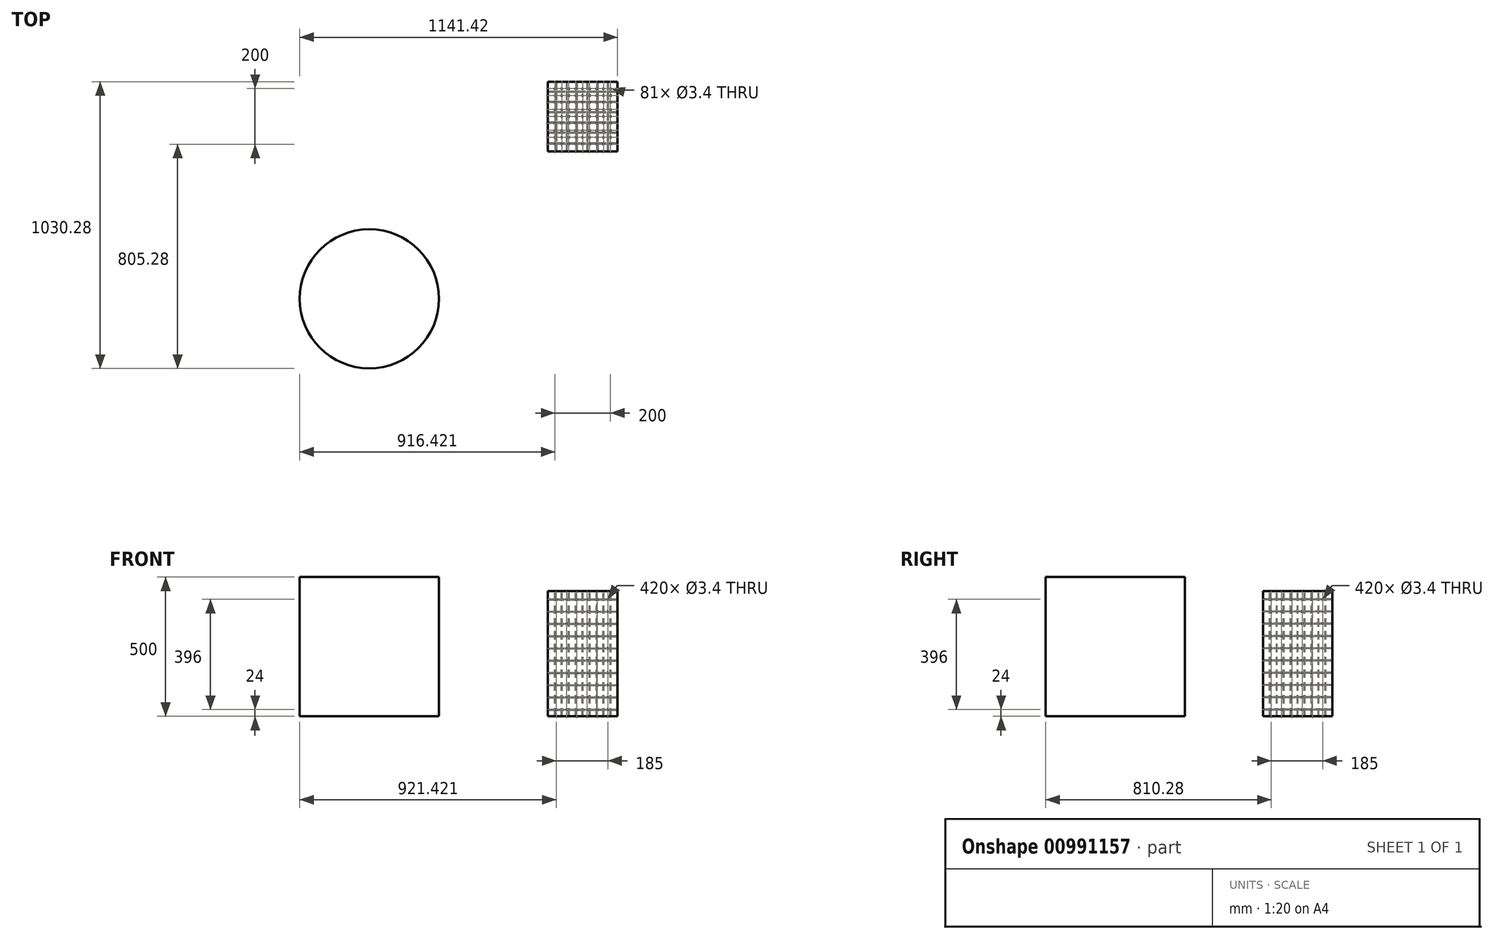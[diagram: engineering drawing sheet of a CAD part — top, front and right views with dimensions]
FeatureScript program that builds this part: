
annotation { "Feature Type Name" : "Feature", "Feature Type Description" : "" }
export const myFeature = defineFeature(function(context is Context, id is Id, definition is map)
    precondition{}
    {
        {
            var Q0;
            Q0=qCreatedBy(makeId("Top.planeOp"),FACE);
            var sketch = newSketch(context, id + "F0", { "sketchPlane" : qUnion([Q0])});
            skLineSegment(sketch, "E0.bottom", {"start": v(256.48, 280.26) * mm, "end": v(6.48, 280.26) * mm});
            skLineSegment(sketch, "E0.top", {"start": v(256.48, 30.26) * mm, "end": v(6.48, 30.26) * mm});
            skLineSegment(sketch, "E0.left", {"start": v(256.48, 280.26) * mm, "end": v(256.48, 30.26) * mm});
            skLineSegment(sketch, "E0.right", {"start": v(6.48, 280.26) * mm, "end": v(6.48, 30.26) * mm});
            skPoint(sketch, "E0.middle", {"position": v(131.48, 155.26) * mm});
            skSolve(sketch);
        }
        {
            var Q0;
            Q0 = qSketchRegion(id + "F0", true);
            extrude(context, id + "F1", {"entities" : qUnion([Q0]), "depth" : 450 * mm, "offsetDistance" : 25 * mm});
        }
        {
            var Q0;
            Q0=makeQuery(id+"F1.opExtrude","SWEPT_FACE",FACE,{"disambiguationData":[OSD([sQuery(id+"F0.wireOp",EDGE,"E0.top")])]});
            var sketch = newSketch(context, id + "F2", { "sketchPlane" : qUnion([Q0])});
            skPoint(sketch, "E1", {"position": v(36.48, 420) * mm});
            skPoint(sketch, "E2.0.1.0", {"position": v(36.48, 376) * mm});
            skPoint(sketch, "E2.0.2.0", {"position": v(36.48, 332) * mm});
            skPoint(sketch, "E2.0.3.0", {"position": v(36.48, 288) * mm});
            skPoint(sketch, "E2.0.4.0", {"position": v(36.48, 244) * mm});
            skPoint(sketch, "E2.0.5.0", {"position": v(36.48, 200) * mm});
            skPoint(sketch, "E2.0.6.0", {"position": v(36.48, 156) * mm});
            skPoint(sketch, "E2.0.7.0", {"position": v(36.48, 112) * mm});
            skPoint(sketch, "E2.0.8.0", {"position": v(36.48, 68) * mm});
            skPoint(sketch, "E2.0.9.0", {"position": v(36.48, 24) * mm});
            skPoint(sketch, "E2.1.0.0", {"position": v(73.48, 420) * mm});
            skPoint(sketch, "E2.1.1.0", {"position": v(73.48, 376) * mm});
            skPoint(sketch, "E2.1.2.0", {"position": v(73.48, 332) * mm});
            skPoint(sketch, "E2.1.3.0", {"position": v(73.48, 288) * mm});
            skPoint(sketch, "E2.1.4.0", {"position": v(73.48, 244) * mm});
            skPoint(sketch, "E2.1.5.0", {"position": v(73.48, 200) * mm});
            skPoint(sketch, "E2.1.6.0", {"position": v(73.48, 156) * mm});
            skPoint(sketch, "E2.1.7.0", {"position": v(73.48, 112) * mm});
            skPoint(sketch, "E2.1.8.0", {"position": v(73.48, 68) * mm});
            skPoint(sketch, "E2.1.9.0", {"position": v(73.48, 24) * mm});
            skPoint(sketch, "E2.2.0.0", {"position": v(110.48, 420) * mm});
            skPoint(sketch, "E2.2.1.0", {"position": v(110.48, 376) * mm});
            skPoint(sketch, "E2.2.2.0", {"position": v(110.48, 332) * mm});
            skPoint(sketch, "E2.2.3.0", {"position": v(110.48, 288) * mm});
            skPoint(sketch, "E2.2.4.0", {"position": v(110.48, 244) * mm});
            skPoint(sketch, "E2.2.5.0", {"position": v(110.48, 200) * mm});
            skPoint(sketch, "E2.2.6.0", {"position": v(110.48, 156) * mm});
            skPoint(sketch, "E2.2.7.0", {"position": v(110.48, 112) * mm});
            skPoint(sketch, "E2.2.8.0", {"position": v(110.48, 68) * mm});
            skPoint(sketch, "E2.2.9.0", {"position": v(110.48, 24) * mm});
            skPoint(sketch, "E2.3.0.0", {"position": v(147.48, 420) * mm});
            skPoint(sketch, "E2.3.1.0", {"position": v(147.48, 376) * mm});
            skPoint(sketch, "E2.3.2.0", {"position": v(147.48, 332) * mm});
            skPoint(sketch, "E2.3.3.0", {"position": v(147.48, 288) * mm});
            skPoint(sketch, "E2.3.4.0", {"position": v(147.48, 244) * mm});
            skPoint(sketch, "E2.3.5.0", {"position": v(147.48, 200) * mm});
            skPoint(sketch, "E2.3.6.0", {"position": v(147.48, 156) * mm});
            skPoint(sketch, "E2.3.7.0", {"position": v(147.48, 112) * mm});
            skPoint(sketch, "E2.3.8.0", {"position": v(147.48, 68) * mm});
            skPoint(sketch, "E2.3.9.0", {"position": v(147.48, 24) * mm});
            skPoint(sketch, "E2.4.0.0", {"position": v(184.48, 420) * mm});
            skPoint(sketch, "E2.4.1.0", {"position": v(184.48, 376) * mm});
            skPoint(sketch, "E2.4.2.0", {"position": v(184.48, 332) * mm});
            skPoint(sketch, "E2.4.3.0", {"position": v(184.48, 288) * mm});
            skPoint(sketch, "E2.4.4.0", {"position": v(184.48, 244) * mm});
            skPoint(sketch, "E2.4.5.0", {"position": v(184.48, 200) * mm});
            skPoint(sketch, "E2.4.6.0", {"position": v(184.48, 156) * mm});
            skPoint(sketch, "E2.4.7.0", {"position": v(184.48, 112) * mm});
            skPoint(sketch, "E2.4.8.0", {"position": v(184.48, 68) * mm});
            skPoint(sketch, "E2.4.9.0", {"position": v(184.48, 24) * mm});
            skPoint(sketch, "E2.5.0.0", {"position": v(221.48, 420) * mm});
            skPoint(sketch, "E2.5.1.0", {"position": v(221.48, 376) * mm});
            skPoint(sketch, "E2.5.2.0", {"position": v(221.48, 332) * mm});
            skPoint(sketch, "E2.5.3.0", {"position": v(221.48, 288) * mm});
            skPoint(sketch, "E2.5.4.0", {"position": v(221.48, 244) * mm});
            skPoint(sketch, "E2.5.5.0", {"position": v(221.48, 200) * mm});
            skPoint(sketch, "E2.5.6.0", {"position": v(221.48, 156) * mm});
            skPoint(sketch, "E2.5.7.0", {"position": v(221.48, 112) * mm});
            skPoint(sketch, "E2.5.8.0", {"position": v(221.48, 68) * mm});
            skPoint(sketch, "E2.5.9.0", {"position": v(221.48, 24) * mm});
            skLineSegment(sketch, "E2.direction1", {"start": v(36.48, 420) * mm, "end": v(73.48, 420) * mm, "construction": true});
            skLineSegment(sketch, "E2.direction2", {"start": v(36.48, 420) * mm, "end": v(36.48, 376) * mm, "construction": true});
            skSolve(sketch);
        }
        {
            var Q0;
            Q0=sQuery(id+"F2.wireOp",VERTEX,"E2.2.6.0");
            var Q1;
            Q1=sQuery(id+"F2.wireOp",VERTEX,"E2.2.5.0");
            var Q2;
            Q2=sQuery(id+"F2.wireOp",VERTEX,"E2.5.8.0");
            var Q3;
            Q3=sQuery(id+"F2.wireOp",VERTEX,"E2.4.2.0");
            var Q4;
            Q4=sQuery(id+"F2.wireOp",VERTEX,"E2.2.4.0");
            var Q5;
            Q5=sQuery(id+"F2.wireOp",VERTEX,"E1");
            var Q6;
            Q6=sQuery(id+"F2.wireOp",VERTEX,"E2.5.7.0");
            var Q7;
            Q7=sQuery(id+"F2.wireOp",VERTEX,"E2.4.1.0");
            var Q8;
            Q8=sQuery(id+"F2.wireOp",VERTEX,"E2.2.3.0");
            var Q9;
            Q9=sQuery(id+"F2.wireOp",VERTEX,"E2.0.1.0");
            var Q10;
            Q10=sQuery(id+"F2.wireOp",VERTEX,"E2.5.6.0");
            var Q11;
            Q11=sQuery(id+"F2.wireOp",VERTEX,"E2.4.0.0");
            var Q12;
            Q12=sQuery(id+"F2.wireOp",VERTEX,"E2.2.2.0");
            var Q13;
            Q13=sQuery(id+"F2.wireOp",VERTEX,"E2.0.2.0");
            var Q14;
            Q14=sQuery(id+"F2.wireOp",VERTEX,"E2.5.5.0");
            var Q15;
            Q15=sQuery(id+"F2.wireOp",VERTEX,"E2.3.9.0");
            var Q16;
            Q16=sQuery(id+"F2.wireOp",VERTEX,"E2.2.1.0");
            var Q17;
            Q17=sQuery(id+"F2.wireOp",VERTEX,"E2.0.3.0");
            var Q18;
            Q18=sQuery(id+"F2.wireOp",VERTEX,"E2.5.4.0");
            var Q19;
            Q19=sQuery(id+"F2.wireOp",VERTEX,"E2.3.8.0");
            var Q20;
            Q20=sQuery(id+"F2.wireOp",VERTEX,"E2.2.0.0");
            var Q21;
            Q21=sQuery(id+"F2.wireOp",VERTEX,"E2.5.3.0");
            var Q22;
            Q22=sQuery(id+"F2.wireOp",VERTEX,"E2.3.7.0");
            var Q23;
            Q23=sQuery(id+"F2.wireOp",VERTEX,"E2.0.4.0");
            var Q24;
            Q24=sQuery(id+"F2.wireOp",VERTEX,"E2.0.5.0");
            var Q25;
            Q25=sQuery(id+"F2.wireOp",VERTEX,"E2.4.4.0");
            var Q26;
            Q26=sQuery(id+"F2.wireOp",VERTEX,"E2.5.1.0");
            var Q27;
            Q27=sQuery(id+"F2.wireOp",VERTEX,"E2.3.5.0");
            var Q28;
            Q28=sQuery(id+"F2.wireOp",VERTEX,"E2.2.8.0");
            var Q29;
            Q29=sQuery(id+"F2.wireOp",VERTEX,"E2.1.9.0");
            var Q30;
            Q30=sQuery(id+"F2.wireOp",VERTEX,"E2.0.6.0");
            var Q31;
            Q31=sQuery(id+"F2.wireOp",VERTEX,"E2.4.3.0");
            var Q32;
            Q32=sQuery(id+"F2.wireOp",VERTEX,"E2.5.0.0");
            var Q33;
            Q33=sQuery(id+"F2.wireOp",VERTEX,"E2.3.4.0");
            var Q34;
            Q34=sQuery(id+"F2.wireOp",VERTEX,"E2.2.7.0");
            var Q35;
            Q35=sQuery(id+"F2.wireOp",VERTEX,"E2.1.8.0");
            var Q36;
            Q36=sQuery(id+"F2.wireOp",VERTEX,"E2.0.7.0");
            var Q37;
            Q37=sQuery(id+"F2.wireOp",VERTEX,"E2.4.9.0");
            var Q38;
            Q38=sQuery(id+"F2.wireOp",VERTEX,"E2.4.5.0");
            var Q39;
            Q39=sQuery(id+"F2.wireOp",VERTEX,"E2.3.3.0");
            var Q40;
            Q40=sQuery(id+"F2.wireOp",VERTEX,"E2.2.9.0");
            var Q41;
            Q41=sQuery(id+"F2.wireOp",VERTEX,"E2.1.7.0");
            var Q42;
            Q42=sQuery(id+"F2.wireOp",VERTEX,"E2.5.9.0");
            var Q43;
            Q43=sQuery(id+"F2.wireOp",VERTEX,"E2.0.8.0");
            var Q44;
            Q44=sQuery(id+"F2.wireOp",VERTEX,"E2.4.8.0");
            var Q45;
            Q45=sQuery(id+"F2.wireOp",VERTEX,"E2.3.2.0");
            var Q46;
            Q46=sQuery(id+"F2.wireOp",VERTEX,"E2.1.6.0");
            var Q47;
            Q47=sQuery(id+"F2.wireOp",VERTEX,"E2.0.9.0");
            var Q48;
            Q48=sQuery(id+"F2.wireOp",VERTEX,"E2.4.7.0");
            var Q49;
            Q49=sQuery(id+"F2.wireOp",VERTEX,"E2.3.1.0");
            var Q50;
            Q50=sQuery(id+"F2.wireOp",VERTEX,"E2.1.5.0");
            var Q51;
            Q51=sQuery(id+"F2.wireOp",VERTEX,"E2.1.0.0");
            var Q52;
            Q52=sQuery(id+"F2.wireOp",VERTEX,"E2.4.6.0");
            var Q53;
            Q53=sQuery(id+"F2.wireOp",VERTEX,"E2.3.0.0");
            var Q54;
            Q54=sQuery(id+"F2.wireOp",VERTEX,"E2.1.4.0");
            var Q55;
            Q55=sQuery(id+"F2.wireOp",VERTEX,"E2.5.2.0");
            var Q56;
            Q56=sQuery(id+"F2.wireOp",VERTEX,"E2.3.6.0");
            var Q57;
            Q57=sQuery(id+"F2.wireOp",VERTEX,"E2.1.3.0");
            var Q58;
            Q58=sQuery(id+"F2.wireOp",VERTEX,"E2.1.1.0");
            var Q59;
            Q59=sQuery(id+"F2.wireOp",VERTEX,"E2.1.2.0");
            var Q60;
            Q60=makeQuery(id+"F1.opExtrude","SWEPT_BODY",BODY,{"disambiguationData":[OSD([sQuery(id+"F0.wireOp",EDGE,"E0.bottom"),sQuery(id+"F0.wireOp",EDGE,"E0.top"),sQuery(id+"F0.wireOp",EDGE,"E0.left"),sQuery(id+"F0.wireOp",EDGE,"E0.right")])]});
            hole(context, id + "F3", {"style" : HoleStyle.SIMPLE, "endStyle" : HoleEndStyle.THROUGH, "standardTappedOrClearance" : lookupTablePath({ "fit" : "Normal", "standard" : "ISO", "size" : "M3", "type" : "Clearance" }), "standardBlindInLast" : lookupTablePath({ "fit" : "Normal", "standard" : "ISO", "engagement" : "75%", "pitch" : "0.5 mm", "size" : "M3", "type" : "Clearance & tapped" }), "holeDiameter" : 3.4 * mm, "majorDiameter" : 5 * mm, "isTappedThrough" : true, "tappedDepth" : 12 * mm, "tapClearance" : 3, "locations" : qUnion([Q0, Q1, Q2, Q3, Q4, Q5, Q6, Q7, Q8, Q9, Q10, Q11, Q12, Q13, Q14, Q15, Q16, Q17, Q18, Q19, Q20, Q21, Q22, Q23, Q24, Q25, Q26, Q27, Q28, Q29, Q30, Q31, Q32, Q33, Q34, Q35, Q36, Q37, Q38, Q39, Q40, Q41, Q42, Q43, Q44, Q45, Q46, Q47, Q48, Q49, Q50, Q51, Q52, Q53, Q54, Q55, Q56, Q57, Q58, Q59]), "scope" : qUnion([Q60])});
        }
        {
            var Q0;
            Q0=makeQuery(id+"F1.opExtrude","SWEPT_FACE",FACE,{"disambiguationData":[OSD([sQuery(id+"F0.wireOp",EDGE,"E0.left")])]});
            var sketch = newSketch(context, id + "F4", { "sketchPlane" : qUnion([Q0])});
            skPoint(sketch, "E3", {"position": v(60.26, 420) * mm});
            skPoint(sketch, "E4.0.1.0", {"position": v(60.26, 376) * mm});
            skPoint(sketch, "E4.0.2.0", {"position": v(60.26, 332) * mm});
            skPoint(sketch, "E4.0.3.0", {"position": v(60.26, 288) * mm});
            skPoint(sketch, "E4.0.4.0", {"position": v(60.26, 244) * mm});
            skPoint(sketch, "E4.0.5.0", {"position": v(60.26, 200) * mm});
            skPoint(sketch, "E4.0.6.0", {"position": v(60.26, 156) * mm});
            skPoint(sketch, "E4.0.7.0", {"position": v(60.26, 112) * mm});
            skPoint(sketch, "E4.0.8.0", {"position": v(60.26, 68) * mm});
            skPoint(sketch, "E4.0.9.0", {"position": v(60.26, 24) * mm});
            skPoint(sketch, "E4.1.0.0", {"position": v(97.26, 420) * mm});
            skPoint(sketch, "E4.1.1.0", {"position": v(97.26, 376) * mm});
            skPoint(sketch, "E4.1.2.0", {"position": v(97.26, 332) * mm});
            skPoint(sketch, "E4.1.3.0", {"position": v(97.26, 288) * mm});
            skPoint(sketch, "E4.1.4.0", {"position": v(97.26, 244) * mm});
            skPoint(sketch, "E4.1.5.0", {"position": v(97.26, 200) * mm});
            skPoint(sketch, "E4.1.6.0", {"position": v(97.26, 156) * mm});
            skPoint(sketch, "E4.1.7.0", {"position": v(97.26, 112) * mm});
            skPoint(sketch, "E4.1.8.0", {"position": v(97.26, 68) * mm});
            skPoint(sketch, "E4.1.9.0", {"position": v(97.26, 24) * mm});
            skPoint(sketch, "E4.2.0.0", {"position": v(134.26, 420) * mm});
            skPoint(sketch, "E4.2.1.0", {"position": v(134.26, 376) * mm});
            skPoint(sketch, "E4.2.2.0", {"position": v(134.26, 332) * mm});
            skPoint(sketch, "E4.2.3.0", {"position": v(134.26, 288) * mm});
            skPoint(sketch, "E4.2.4.0", {"position": v(134.26, 244) * mm});
            skPoint(sketch, "E4.2.5.0", {"position": v(134.26, 200) * mm});
            skPoint(sketch, "E4.2.6.0", {"position": v(134.26, 156) * mm});
            skPoint(sketch, "E4.2.7.0", {"position": v(134.26, 112) * mm});
            skPoint(sketch, "E4.2.8.0", {"position": v(134.26, 68) * mm});
            skPoint(sketch, "E4.2.9.0", {"position": v(134.26, 24) * mm});
            skPoint(sketch, "E4.3.0.0", {"position": v(171.26, 420) * mm});
            skPoint(sketch, "E4.3.1.0", {"position": v(171.26, 376) * mm});
            skPoint(sketch, "E4.3.2.0", {"position": v(171.26, 332) * mm});
            skPoint(sketch, "E4.3.3.0", {"position": v(171.26, 288) * mm});
            skPoint(sketch, "E4.3.4.0", {"position": v(171.26, 244) * mm});
            skPoint(sketch, "E4.3.5.0", {"position": v(171.26, 200) * mm});
            skPoint(sketch, "E4.3.6.0", {"position": v(171.26, 156) * mm});
            skPoint(sketch, "E4.3.7.0", {"position": v(171.26, 112) * mm});
            skPoint(sketch, "E4.3.8.0", {"position": v(171.26, 68) * mm});
            skPoint(sketch, "E4.3.9.0", {"position": v(171.26, 24) * mm});
            skPoint(sketch, "E4.4.0.0", {"position": v(208.26, 420) * mm});
            skPoint(sketch, "E4.4.1.0", {"position": v(208.26, 376) * mm});
            skPoint(sketch, "E4.4.2.0", {"position": v(208.26, 332) * mm});
            skPoint(sketch, "E4.4.3.0", {"position": v(208.26, 288) * mm});
            skPoint(sketch, "E4.4.4.0", {"position": v(208.26, 244) * mm});
            skPoint(sketch, "E4.4.5.0", {"position": v(208.26, 200) * mm});
            skPoint(sketch, "E4.4.6.0", {"position": v(208.26, 156) * mm});
            skPoint(sketch, "E4.4.7.0", {"position": v(208.26, 112) * mm});
            skPoint(sketch, "E4.4.8.0", {"position": v(208.26, 68) * mm});
            skPoint(sketch, "E4.4.9.0", {"position": v(208.26, 24) * mm});
            skPoint(sketch, "E4.5.0.0", {"position": v(245.26, 420) * mm});
            skPoint(sketch, "E4.5.1.0", {"position": v(245.26, 376) * mm});
            skPoint(sketch, "E4.5.2.0", {"position": v(245.26, 332) * mm});
            skPoint(sketch, "E4.5.3.0", {"position": v(245.26, 288) * mm});
            skPoint(sketch, "E4.5.4.0", {"position": v(245.26, 244) * mm});
            skPoint(sketch, "E4.5.5.0", {"position": v(245.26, 200) * mm});
            skPoint(sketch, "E4.5.6.0", {"position": v(245.26, 156) * mm});
            skPoint(sketch, "E4.5.7.0", {"position": v(245.26, 112) * mm});
            skPoint(sketch, "E4.5.8.0", {"position": v(245.26, 68) * mm});
            skPoint(sketch, "E4.5.9.0", {"position": v(245.26, 24) * mm});
            skLineSegment(sketch, "E4.direction1", {"start": v(60.26, 420) * mm, "end": v(97.26, 420) * mm, "construction": true});
            skLineSegment(sketch, "E4.direction2", {"start": v(60.26, 420) * mm, "end": v(60.26, 376) * mm, "construction": true});
            skSolve(sketch);
        }
        {
            var Q0;
            Q0=sQuery(id+"F4.wireOp",VERTEX,"E4.1.2.0");
            var Q1;
            Q1=sQuery(id+"F4.wireOp",VERTEX,"E4.0.8.0");
            var Q2;
            Q2=sQuery(id+"F4.wireOp",VERTEX,"E4.2.7.0");
            var Q3;
            Q3=sQuery(id+"F4.wireOp",VERTEX,"E4.3.7.0");
            var Q4;
            Q4=sQuery(id+"F4.wireOp",VERTEX,"E4.2.4.0");
            var Q5;
            Q5=sQuery(id+"F4.wireOp",VERTEX,"E4.2.8.0");
            var Q6;
            Q6=sQuery(id+"F4.wireOp",VERTEX,"E4.5.7.0");
            var Q7;
            Q7=sQuery(id+"F4.wireOp",VERTEX,"E4.4.9.0");
            var Q8;
            Q8=sQuery(id+"F4.wireOp",VERTEX,"E4.5.2.0");
            var Q9;
            Q9=sQuery(id+"F4.wireOp",VERTEX,"E4.3.0.0");
            var Q10;
            Q10=sQuery(id+"F4.wireOp",VERTEX,"E4.1.8.0");
            var Q11;
            Q11=sQuery(id+"F4.wireOp",VERTEX,"E4.2.5.0");
            var Q12;
            Q12=sQuery(id+"F4.wireOp",VERTEX,"E4.1.0.0");
            var Q13;
            Q13=sQuery(id+"F4.wireOp",VERTEX,"E4.4.6.0");
            var Q14;
            Q14=sQuery(id+"F4.wireOp",VERTEX,"E4.1.6.0");
            var Q15;
            Q15=sQuery(id+"F4.wireOp",VERTEX,"E4.0.5.0");
            var Q16;
            Q16=sQuery(id+"F4.wireOp",VERTEX,"E4.0.6.0");
            var Q17;
            Q17=sQuery(id+"F4.wireOp",VERTEX,"E3");
            var Q18;
            Q18=sQuery(id+"F4.wireOp",VERTEX,"E4.5.1.0");
            var Q19;
            Q19=sQuery(id+"F4.wireOp",VERTEX,"E4.2.1.0");
            var Q20;
            Q20=sQuery(id+"F4.wireOp",VERTEX,"E4.0.3.0");
            var Q21;
            Q21=sQuery(id+"F4.wireOp",VERTEX,"E4.5.8.0");
            var Q22;
            Q22=sQuery(id+"F4.wireOp",VERTEX,"E4.5.9.0");
            var Q23;
            Q23=sQuery(id+"F4.wireOp",VERTEX,"E4.2.0.0");
            var Q24;
            Q24=sQuery(id+"F4.wireOp",VERTEX,"E4.1.1.0");
            var Q25;
            Q25=sQuery(id+"F4.wireOp",VERTEX,"E4.2.2.0");
            var Q26;
            Q26=sQuery(id+"F4.wireOp",VERTEX,"E4.3.2.0");
            var Q27;
            Q27=sQuery(id+"F4.wireOp",VERTEX,"E4.3.9.0");
            var Q28;
            Q28=sQuery(id+"F4.wireOp",VERTEX,"E4.5.4.0");
            var Q29;
            Q29=sQuery(id+"F4.wireOp",VERTEX,"E4.4.3.0");
            var Q30;
            Q30=sQuery(id+"F4.wireOp",VERTEX,"E4.1.4.0");
            var Q31;
            Q31=sQuery(id+"F4.wireOp",VERTEX,"E4.1.3.0");
            var Q32;
            Q32=sQuery(id+"F4.wireOp",VERTEX,"E4.0.7.0");
            var Q33;
            Q33=sQuery(id+"F4.wireOp",VERTEX,"E4.2.3.0");
            var Q34;
            Q34=sQuery(id+"F4.wireOp",VERTEX,"E4.5.5.0");
            var Q35;
            Q35=sQuery(id+"F4.wireOp",VERTEX,"E4.3.4.0");
            var Q36;
            Q36=sQuery(id+"F4.wireOp",VERTEX,"E4.5.6.0");
            var Q37;
            Q37=sQuery(id+"F4.wireOp",VERTEX,"E4.4.4.0");
            var Q38;
            Q38=sQuery(id+"F4.wireOp",VERTEX,"E4.4.2.0");
            var Q39;
            Q39=sQuery(id+"F4.wireOp",VERTEX,"E4.5.0.0");
            var Q40;
            Q40=sQuery(id+"F4.wireOp",VERTEX,"E4.0.4.0");
            var Q41;
            Q41=sQuery(id+"F4.wireOp",VERTEX,"E4.4.0.0");
            var Q42;
            Q42=sQuery(id+"F4.wireOp",VERTEX,"E4.1.9.0");
            var Q43;
            Q43=sQuery(id+"F4.wireOp",VERTEX,"E4.1.7.0");
            var Q44;
            Q44=sQuery(id+"F4.wireOp",VERTEX,"E4.3.5.0");
            var Q45;
            Q45=sQuery(id+"F4.wireOp",VERTEX,"E4.2.9.0");
            var Q46;
            Q46=sQuery(id+"F4.wireOp",VERTEX,"E4.1.5.0");
            var Q47;
            Q47=sQuery(id+"F4.wireOp",VERTEX,"E4.4.5.0");
            var Q48;
            Q48=sQuery(id+"F4.wireOp",VERTEX,"E4.4.8.0");
            var Q49;
            Q49=sQuery(id+"F4.wireOp",VERTEX,"E4.3.8.0");
            var Q50;
            Q50=sQuery(id+"F4.wireOp",VERTEX,"E4.3.1.0");
            var Q51;
            Q51=sQuery(id+"F4.wireOp",VERTEX,"E4.3.3.0");
            var Q52;
            Q52=sQuery(id+"F4.wireOp",VERTEX,"E4.4.7.0");
            var Q53;
            Q53=sQuery(id+"F4.wireOp",VERTEX,"E4.0.9.0");
            var Q54;
            Q54=sQuery(id+"F4.wireOp",VERTEX,"E4.2.6.0");
            var Q55;
            Q55=sQuery(id+"F4.wireOp",VERTEX,"E4.3.6.0");
            var Q56;
            Q56=sQuery(id+"F4.wireOp",VERTEX,"E4.0.2.0");
            var Q57;
            Q57=sQuery(id+"F4.wireOp",VERTEX,"E4.5.3.0");
            var Q58;
            Q58=sQuery(id+"F4.wireOp",VERTEX,"E4.4.1.0");
            var Q59;
            Q59=sQuery(id+"F4.wireOp",VERTEX,"E4.0.1.0");
            var Q60;
            Q60=makeQuery(id+"F1.opExtrude","SWEPT_BODY",BODY,{"disambiguationData":[OSD([sQuery(id+"F0.wireOp",EDGE,"E0.bottom"),sQuery(id+"F0.wireOp",EDGE,"E0.top"),sQuery(id+"F0.wireOp",EDGE,"E0.left"),sQuery(id+"F0.wireOp",EDGE,"E0.right")])]});
            hole(context, id + "F5", {"style" : HoleStyle.SIMPLE, "endStyle" : HoleEndStyle.THROUGH, "standardTappedOrClearance" : lookupTablePath({ "fit" : "Normal", "standard" : "ISO", "size" : "M3", "type" : "Clearance" }), "standardBlindInLast" : lookupTablePath({ "fit" : "Normal", "standard" : "ISO", "engagement" : "75%", "pitch" : "0.5 mm", "size" : "M3", "type" : "Clearance & tapped" }), "holeDiameter" : 3.4 * mm, "majorDiameter" : 5 * mm, "isTappedThrough" : true, "tappedDepth" : 12 * mm, "tapClearance" : 3, "locations" : qUnion([Q0, Q1, Q2, Q3, Q4, Q5, Q6, Q7, Q8, Q9, Q10, Q11, Q12, Q13, Q14, Q15, Q16, Q17, Q18, Q19, Q20, Q21, Q22, Q23, Q24, Q25, Q26, Q27, Q28, Q29, Q30, Q31, Q32, Q33, Q34, Q35, Q36, Q37, Q38, Q39, Q40, Q41, Q42, Q43, Q44, Q45, Q46, Q47, Q48, Q49, Q50, Q51, Q52, Q53, Q54, Q55, Q56, Q57, Q58, Q59]), "scope" : qUnion([Q60])});
        }
        {
            var Q0;
            Q0=makeQuery(id+"F1.opExtrude","CAP_FACE",FACE,{"disambiguationData":[OSD([sQuery(id+"F0.wireOp",EDGE,"E0.bottom"),sQuery(id+"F0.wireOp",EDGE,"E0.top"),sQuery(id+"F0.wireOp",EDGE,"E0.left"),sQuery(id+"F0.wireOp",EDGE,"E0.right")])],"isStart":false});
            var sketch = newSketch(context, id + "F6", { "sketchPlane" : qUnion([Q0])});
            skPoint(sketch, "E5", {"position": v(31.48, 255.26) * mm});
            skPoint(sketch, "E6.0.1.0", {"position": v(31.48, 230.26) * mm});
            skPoint(sketch, "E6.0.2.0", {"position": v(31.48, 205.26) * mm});
            skPoint(sketch, "E6.0.3.0", {"position": v(31.48, 180.26) * mm});
            skPoint(sketch, "E6.0.4.0", {"position": v(31.48, 155.26) * mm});
            skPoint(sketch, "E6.0.5.0", {"position": v(31.48, 130.26) * mm});
            skPoint(sketch, "E6.0.6.0", {"position": v(31.48, 105.26) * mm});
            skPoint(sketch, "E6.0.7.0", {"position": v(31.48, 80.26) * mm});
            skPoint(sketch, "E6.0.8.0", {"position": v(31.48, 55.26) * mm});
            skPoint(sketch, "E6.1.0.0", {"position": v(56.48, 255.26) * mm});
            skPoint(sketch, "E6.1.1.0", {"position": v(56.48, 230.26) * mm});
            skPoint(sketch, "E6.1.2.0", {"position": v(56.48, 205.26) * mm});
            skPoint(sketch, "E6.1.3.0", {"position": v(56.48, 180.26) * mm});
            skPoint(sketch, "E6.1.4.0", {"position": v(56.48, 155.26) * mm});
            skPoint(sketch, "E6.1.5.0", {"position": v(56.48, 130.26) * mm});
            skPoint(sketch, "E6.1.6.0", {"position": v(56.48, 105.26) * mm});
            skPoint(sketch, "E6.1.7.0", {"position": v(56.48, 80.26) * mm});
            skPoint(sketch, "E6.1.8.0", {"position": v(56.48, 55.26) * mm});
            skPoint(sketch, "E6.2.0.0", {"position": v(81.48, 255.26) * mm});
            skPoint(sketch, "E6.2.1.0", {"position": v(81.48, 230.26) * mm});
            skPoint(sketch, "E6.2.2.0", {"position": v(81.48, 205.26) * mm});
            skPoint(sketch, "E6.2.3.0", {"position": v(81.48, 180.26) * mm});
            skPoint(sketch, "E6.2.4.0", {"position": v(81.48, 155.26) * mm});
            skPoint(sketch, "E6.2.5.0", {"position": v(81.48, 130.26) * mm});
            skPoint(sketch, "E6.2.6.0", {"position": v(81.48, 105.26) * mm});
            skPoint(sketch, "E6.2.7.0", {"position": v(81.48, 80.26) * mm});
            skPoint(sketch, "E6.2.8.0", {"position": v(81.48, 55.26) * mm});
            skPoint(sketch, "E6.3.0.0", {"position": v(106.48, 255.26) * mm});
            skPoint(sketch, "E6.3.1.0", {"position": v(106.48, 230.26) * mm});
            skPoint(sketch, "E6.3.2.0", {"position": v(106.48, 205.26) * mm});
            skPoint(sketch, "E6.3.3.0", {"position": v(106.48, 180.26) * mm});
            skPoint(sketch, "E6.3.4.0", {"position": v(106.48, 155.26) * mm});
            skPoint(sketch, "E6.3.5.0", {"position": v(106.48, 130.26) * mm});
            skPoint(sketch, "E6.3.6.0", {"position": v(106.48, 105.26) * mm});
            skPoint(sketch, "E6.3.7.0", {"position": v(106.48, 80.26) * mm});
            skPoint(sketch, "E6.3.8.0", {"position": v(106.48, 55.26) * mm});
            skPoint(sketch, "E6.4.0.0", {"position": v(131.48, 255.26) * mm});
            skPoint(sketch, "E6.4.1.0", {"position": v(131.48, 230.26) * mm});
            skPoint(sketch, "E6.4.2.0", {"position": v(131.48, 205.26) * mm});
            skPoint(sketch, "E6.4.3.0", {"position": v(131.48, 180.26) * mm});
            skPoint(sketch, "E6.4.4.0", {"position": v(131.48, 155.26) * mm});
            skPoint(sketch, "E6.4.5.0", {"position": v(131.48, 130.26) * mm});
            skPoint(sketch, "E6.4.6.0", {"position": v(131.48, 105.26) * mm});
            skPoint(sketch, "E6.4.7.0", {"position": v(131.48, 80.26) * mm});
            skPoint(sketch, "E6.4.8.0", {"position": v(131.48, 55.26) * mm});
            skPoint(sketch, "E6.5.0.0", {"position": v(156.48, 255.26) * mm});
            skPoint(sketch, "E6.5.1.0", {"position": v(156.48, 230.26) * mm});
            skPoint(sketch, "E6.5.2.0", {"position": v(156.48, 205.26) * mm});
            skPoint(sketch, "E6.5.3.0", {"position": v(156.48, 180.26) * mm});
            skPoint(sketch, "E6.5.4.0", {"position": v(156.48, 155.26) * mm});
            skPoint(sketch, "E6.5.5.0", {"position": v(156.48, 130.26) * mm});
            skPoint(sketch, "E6.5.6.0", {"position": v(156.48, 105.26) * mm});
            skPoint(sketch, "E6.5.7.0", {"position": v(156.48, 80.26) * mm});
            skPoint(sketch, "E6.5.8.0", {"position": v(156.48, 55.26) * mm});
            skPoint(sketch, "E6.6.0.0", {"position": v(181.48, 255.26) * mm});
            skPoint(sketch, "E6.6.1.0", {"position": v(181.48, 230.26) * mm});
            skPoint(sketch, "E6.6.2.0", {"position": v(181.48, 205.26) * mm});
            skPoint(sketch, "E6.6.3.0", {"position": v(181.48, 180.26) * mm});
            skPoint(sketch, "E6.6.4.0", {"position": v(181.48, 155.26) * mm});
            skPoint(sketch, "E6.6.5.0", {"position": v(181.48, 130.26) * mm});
            skPoint(sketch, "E6.6.6.0", {"position": v(181.48, 105.26) * mm});
            skPoint(sketch, "E6.6.7.0", {"position": v(181.48, 80.26) * mm});
            skPoint(sketch, "E6.6.8.0", {"position": v(181.48, 55.26) * mm});
            skPoint(sketch, "E6.7.0.0", {"position": v(206.48, 255.26) * mm});
            skPoint(sketch, "E6.7.1.0", {"position": v(206.48, 230.26) * mm});
            skPoint(sketch, "E6.7.2.0", {"position": v(206.48, 205.26) * mm});
            skPoint(sketch, "E6.7.3.0", {"position": v(206.48, 180.26) * mm});
            skPoint(sketch, "E6.7.4.0", {"position": v(206.48, 155.26) * mm});
            skPoint(sketch, "E6.7.5.0", {"position": v(206.48, 130.26) * mm});
            skPoint(sketch, "E6.7.6.0", {"position": v(206.48, 105.26) * mm});
            skPoint(sketch, "E6.7.7.0", {"position": v(206.48, 80.26) * mm});
            skPoint(sketch, "E6.7.8.0", {"position": v(206.48, 55.26) * mm});
            skPoint(sketch, "E6.8.0.0", {"position": v(231.48, 255.26) * mm});
            skPoint(sketch, "E6.8.1.0", {"position": v(231.48, 230.26) * mm});
            skPoint(sketch, "E6.8.2.0", {"position": v(231.48, 205.26) * mm});
            skPoint(sketch, "E6.8.3.0", {"position": v(231.48, 180.26) * mm});
            skPoint(sketch, "E6.8.4.0", {"position": v(231.48, 155.26) * mm});
            skPoint(sketch, "E6.8.5.0", {"position": v(231.48, 130.26) * mm});
            skPoint(sketch, "E6.8.6.0", {"position": v(231.48, 105.26) * mm});
            skPoint(sketch, "E6.8.7.0", {"position": v(231.48, 80.26) * mm});
            skPoint(sketch, "E6.8.8.0", {"position": v(231.48, 55.26) * mm});
            skLineSegment(sketch, "E6.direction1", {"start": v(31.48, 255.26) * mm, "end": v(56.48, 255.26) * mm, "construction": true});
            skLineSegment(sketch, "E6.direction2", {"start": v(31.48, 255.26) * mm, "end": v(31.48, 230.26) * mm, "construction": true});
            skSolve(sketch);
        }
        {
            var Q0;
            Q0=sQuery(id+"F6.wireOp",VERTEX,"E6.4.4.0");
            var Q1;
            Q1=sQuery(id+"F6.wireOp",VERTEX,"E6.6.2.0");
            var Q2;
            Q2=sQuery(id+"F6.wireOp",VERTEX,"E6.0.2.0");
            var Q3;
            Q3=sQuery(id+"F6.wireOp",VERTEX,"E6.2.6.0");
            var Q4;
            Q4=sQuery(id+"F6.wireOp",VERTEX,"E6.8.1.0");
            var Q5;
            Q5=sQuery(id+"F6.wireOp",VERTEX,"E6.6.1.0");
            var Q6;
            Q6=sQuery(id+"F6.wireOp",VERTEX,"E6.4.3.0");
            var Q7;
            Q7=sQuery(id+"F6.wireOp",VERTEX,"E6.2.5.0");
            var Q8;
            Q8=sQuery(id+"F6.wireOp",VERTEX,"E6.0.1.0");
            var Q9;
            Q9=sQuery(id+"F6.wireOp",VERTEX,"E6.8.0.0");
            var Q10;
            Q10=sQuery(id+"F6.wireOp",VERTEX,"E6.6.0.0");
            var Q11;
            Q11=sQuery(id+"F6.wireOp",VERTEX,"E6.4.2.0");
            var Q12;
            Q12=sQuery(id+"F6.wireOp",VERTEX,"E6.2.4.0");
            var Q13;
            Q13=sQuery(id+"F6.wireOp",VERTEX,"E6.7.8.0");
            var Q14;
            Q14=sQuery(id+"F6.wireOp",VERTEX,"E6.5.8.0");
            var Q15;
            Q15=sQuery(id+"F6.wireOp",VERTEX,"E6.4.1.0");
            var Q16;
            Q16=sQuery(id+"F6.wireOp",VERTEX,"E6.0.3.0");
            var Q17;
            Q17=sQuery(id+"F6.wireOp",VERTEX,"E6.2.3.0");
            var Q18;
            Q18=sQuery(id+"F6.wireOp",VERTEX,"E6.7.7.0");
            var Q19;
            Q19=sQuery(id+"F6.wireOp",VERTEX,"E6.5.7.0");
            var Q20;
            Q20=sQuery(id+"F6.wireOp",VERTEX,"E6.0.5.0");
            var Q21;
            Q21=sQuery(id+"F6.wireOp",VERTEX,"E6.4.0.0");
            var Q22;
            Q22=sQuery(id+"F6.wireOp",VERTEX,"E6.2.2.0");
            var Q23;
            Q23=sQuery(id+"F6.wireOp",VERTEX,"E6.7.6.0");
            var Q24;
            Q24=sQuery(id+"F6.wireOp",VERTEX,"E6.0.4.0");
            var Q25;
            Q25=sQuery(id+"F6.wireOp",VERTEX,"E6.7.5.0");
            var Q26;
            Q26=sQuery(id+"F6.wireOp",VERTEX,"E6.0.7.0");
            var Q27;
            Q27=sQuery(id+"F6.wireOp",VERTEX,"E6.0.6.0");
            var Q28;
            Q28=sQuery(id+"F6.wireOp",VERTEX,"E6.1.3.0");
            var Q29;
            Q29=sQuery(id+"F6.wireOp",VERTEX,"E6.1.2.0");
            var Q30;
            Q30=sQuery(id+"F6.wireOp",VERTEX,"E5");
            var Q31;
            Q31=sQuery(id+"F6.wireOp",VERTEX,"E6.2.1.0");
            var Q32;
            Q32=sQuery(id+"F6.wireOp",VERTEX,"E6.1.4.0");
            var Q33;
            Q33=sQuery(id+"F6.wireOp",VERTEX,"E6.8.4.0");
            var Q34;
            Q34=sQuery(id+"F6.wireOp",VERTEX,"E6.2.0.0");
            var Q35;
            Q35=sQuery(id+"F6.wireOp",VERTEX,"E6.6.6.0");
            var Q36;
            Q36=sQuery(id+"F6.wireOp",VERTEX,"E6.7.4.0");
            var Q37;
            Q37=sQuery(id+"F6.wireOp",VERTEX,"E6.4.8.0");
            var Q38;
            Q38=sQuery(id+"F6.wireOp",VERTEX,"E6.5.6.0");
            var Q39;
            Q39=sQuery(id+"F6.wireOp",VERTEX,"E6.3.8.0");
            var Q40;
            Q40=sQuery(id+"F6.wireOp",VERTEX,"E6.3.1.0");
            var Q41;
            Q41=sQuery(id+"F6.wireOp",VERTEX,"E6.8.3.0");
            var Q42;
            Q42=sQuery(id+"F6.wireOp",VERTEX,"E6.1.8.0");
            var Q43;
            Q43=sQuery(id+"F6.wireOp",VERTEX,"E6.1.0.0");
            var Q44;
            Q44=sQuery(id+"F6.wireOp",VERTEX,"E6.7.3.0");
            var Q45;
            Q45=sQuery(id+"F6.wireOp",VERTEX,"E6.6.5.0");
            var Q46;
            Q46=sQuery(id+"F6.wireOp",VERTEX,"E6.4.7.0");
            var Q47;
            Q47=sQuery(id+"F6.wireOp",VERTEX,"E6.5.5.0");
            var Q48;
            Q48=sQuery(id+"F6.wireOp",VERTEX,"E6.3.7.0");
            var Q49;
            Q49=sQuery(id+"F6.wireOp",VERTEX,"E6.3.0.0");
            var Q50;
            Q50=sQuery(id+"F6.wireOp",VERTEX,"E6.0.8.0");
            var Q51;
            Q51=sQuery(id+"F6.wireOp",VERTEX,"E6.8.5.0");
            var Q52;
            Q52=sQuery(id+"F6.wireOp",VERTEX,"E6.1.7.0");
            var Q53;
            Q53=sQuery(id+"F6.wireOp",VERTEX,"E6.6.7.0");
            var Q54;
            Q54=sQuery(id+"F6.wireOp",VERTEX,"E6.7.2.0");
            var Q55;
            Q55=sQuery(id+"F6.wireOp",VERTEX,"E6.5.4.0");
            var Q56;
            Q56=sQuery(id+"F6.wireOp",VERTEX,"E6.5.0.0");
            var Q57;
            Q57=sQuery(id+"F6.wireOp",VERTEX,"E6.3.2.0");
            var Q58;
            Q58=sQuery(id+"F6.wireOp",VERTEX,"E6.3.6.0");
            var Q59;
            Q59=sQuery(id+"F6.wireOp",VERTEX,"E6.8.8.0");
            var Q60;
            Q60=sQuery(id+"F6.wireOp",VERTEX,"E6.1.6.0");
            var Q61;
            Q61=sQuery(id+"F6.wireOp",VERTEX,"E6.7.1.0");
            var Q62;
            Q62=sQuery(id+"F6.wireOp",VERTEX,"E6.5.3.0");
            var Q63;
            Q63=sQuery(id+"F6.wireOp",VERTEX,"E6.3.5.0");
            var Q64;
            Q64=sQuery(id+"F6.wireOp",VERTEX,"E6.8.7.0");
            var Q65;
            Q65=sQuery(id+"F6.wireOp",VERTEX,"E6.1.5.0");
            var Q66;
            Q66=sQuery(id+"F6.wireOp",VERTEX,"E6.1.1.0");
            var Q67;
            Q67=sQuery(id+"F6.wireOp",VERTEX,"E6.7.0.0");
            var Q68;
            Q68=sQuery(id+"F6.wireOp",VERTEX,"E6.5.2.0");
            var Q69;
            Q69=sQuery(id+"F6.wireOp",VERTEX,"E6.3.4.0");
            var Q70;
            Q70=sQuery(id+"F6.wireOp",VERTEX,"E6.8.6.0");
            var Q71;
            Q71=sQuery(id+"F6.wireOp",VERTEX,"E6.6.8.0");
            var Q72;
            Q72=sQuery(id+"F6.wireOp",VERTEX,"E6.5.1.0");
            var Q73;
            Q73=sQuery(id+"F6.wireOp",VERTEX,"E6.3.3.0");
            var Q74;
            Q74=sQuery(id+"F6.wireOp",VERTEX,"E6.6.4.0");
            var Q75;
            Q75=sQuery(id+"F6.wireOp",VERTEX,"E6.4.6.0");
            var Q76;
            Q76=sQuery(id+"F6.wireOp",VERTEX,"E6.2.8.0");
            var Q77;
            Q77=sQuery(id+"F6.wireOp",VERTEX,"E6.6.3.0");
            var Q78;
            Q78=sQuery(id+"F6.wireOp",VERTEX,"E6.4.5.0");
            var Q79;
            Q79=sQuery(id+"F6.wireOp",VERTEX,"E6.2.7.0");
            var Q80;
            Q80=sQuery(id+"F6.wireOp",VERTEX,"E6.8.2.0");
            var Q81;
            Q81=makeQuery(id+"F1.opExtrude","SWEPT_BODY",BODY,{"disambiguationData":[OSD([sQuery(id+"F0.wireOp",EDGE,"E0.bottom"),sQuery(id+"F0.wireOp",EDGE,"E0.top"),sQuery(id+"F0.wireOp",EDGE,"E0.left"),sQuery(id+"F0.wireOp",EDGE,"E0.right")])]});
            hole(context, id + "F7", {"style" : HoleStyle.SIMPLE, "endStyle" : HoleEndStyle.THROUGH, "standardTappedOrClearance" : lookupTablePath({ "fit" : "Normal", "standard" : "ISO", "size" : "M3", "type" : "Clearance" }), "standardBlindInLast" : lookupTablePath({ "fit" : "Normal", "standard" : "ISO", "engagement" : "75%", "pitch" : "0.5 mm", "size" : "M3", "type" : "Clearance & tapped" }), "holeDiameter" : 3.4 * mm, "majorDiameter" : 5 * mm, "isTappedThrough" : true, "tappedDepth" : 12 * mm, "tapClearance" : 3, "locations" : qUnion([Q0, Q1, Q2, Q3, Q4, Q5, Q6, Q7, Q8, Q9, Q10, Q11, Q12, Q13, Q14, Q15, Q16, Q17, Q18, Q19, Q20, Q21, Q22, Q23, Q24, Q25, Q26, Q27, Q28, Q29, Q30, Q31, Q32, Q33, Q34, Q35, Q36, Q37, Q38, Q39, Q40, Q41, Q42, Q43, Q44, Q45, Q46, Q47, Q48, Q49, Q50, Q51, Q52, Q53, Q54, Q55, Q56, Q57, Q58, Q59, Q60, Q61, Q62, Q63, Q64, Q65, Q66, Q67, Q68, Q69, Q70, Q71, Q72, Q73, Q74, Q75, Q76, Q77, Q78, Q79, Q80]), "scope" : qUnion([Q81])});
        }
        {
            var Q0;
            Q0=qCreatedBy(makeId("Top.planeOp"),FACE);
            var sketch = newSketch(context, id + "F8", { "sketchPlane" : qUnion([Q0])});
            skCircle(sketch, "E7", {"center": v(-634.94, -500.02) * mm, "radius": 250 * mm});
            skSolve(sketch);
        }
        {
            var Q0;
            Q0 = qSketchRegion(id + "F8", true);
            extrude(context, id + "F9", {"entities" : qUnion([Q0]), "depth" : 500 * mm, "offsetDistance" : 25 * mm});
        }
    });
